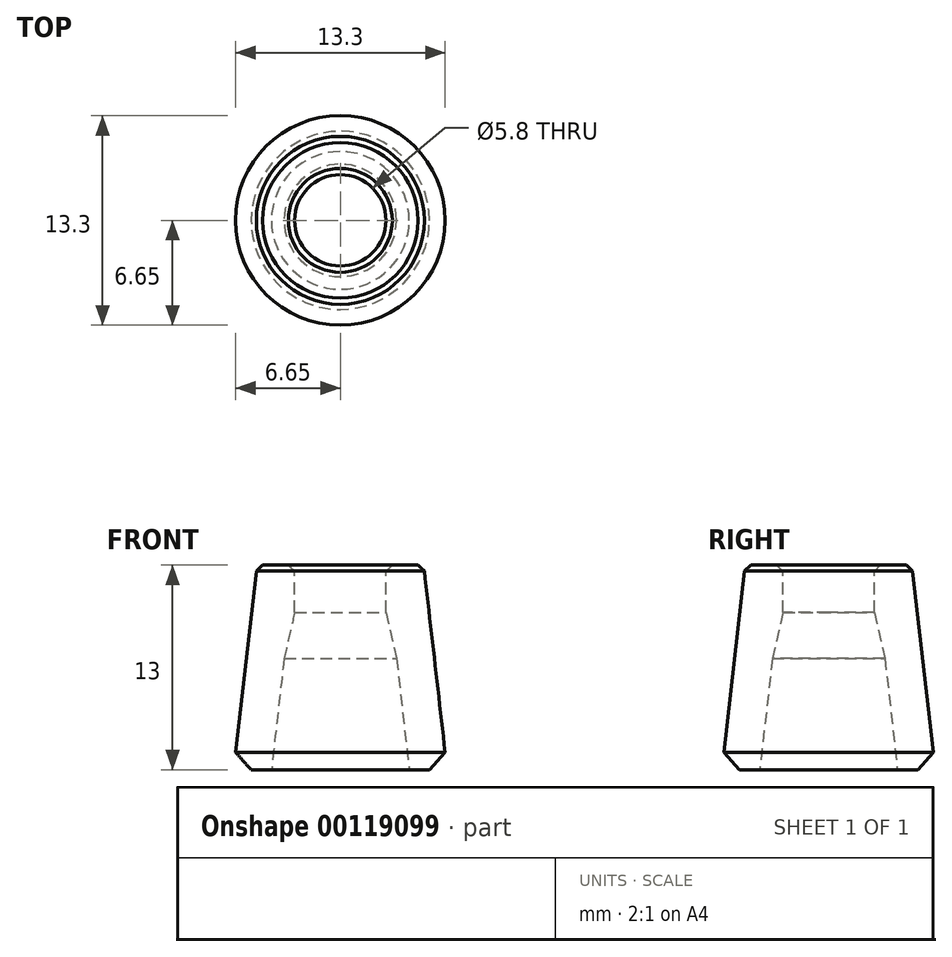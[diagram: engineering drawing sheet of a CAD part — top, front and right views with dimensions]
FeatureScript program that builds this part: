
annotation { "Feature Type Name" : "Feature", "Feature Type Description" : "" }
export const myFeature = defineFeature(function(context is Context, id is Id, definition is map)
    precondition{}
    {
        {
            var Q0;
            Q0=qCreatedBy(makeId("Front.planeOp"),FACE);
            var sketch = newSketch(context, id + "F0", { "sketchPlane" : qUnion([Q0])});
            skLineSegment(sketch, "E0", {"start": v(0, 0) * mm, "end": v(0, 13) * mm, "construction": true});
            skLineSegment(sketch, "E1", {"start": v(2.9, 0) * mm, "end": v(5.3, 0) * mm});
            skLineSegment(sketch, "E2", {"start": v(4.38, 13) * mm, "end": v(3.57, 5.92) * mm});
            skPoint(sketch, "E3.visualSharp", {"position": v(4.37, 13) * mm});
            skLineSegment(sketch, "E4.0", {"start": v(6.78, 13) * mm, "end": v(5.3, 0) * mm});
            skLineSegment(sketch, "E5", {"start": v(2.9, 0) * mm, "end": v(2.9, 3) * mm});
            skLineSegment(sketch, "E6", {"start": v(2.9, 3) * mm, "end": v(3.57, 5.92) * mm});
            skLineSegment(sketch, "E7", {"start": v(4.37, 13) * mm, "end": v(6.78, 13) * mm});
            skPoint(sketch, "E8.orphan", {"position": v(4.24, 11.85) * mm});
            skLineSegment(sketch, "E9", {"start": v(6.78, 13) * mm, "end": v(19.88, 13) * mm, "construction": true});
            skSolve(sketch);
        }
        {
            var Q0;
            Q0=makeQuery(id+"F0.imprint","IMPRINT",FACE,{"disambiguationData":[TD([[makeQuery(id+"F0.imprint","IMPRINT",EDGE,{"derivedFrom":sQuery(id+"F0.wireOp",EDGE,"E1")}),1.0]])]});
            var Q1;
            Q1=sQuery(id+"F0.wireOp",EDGE,"E0");
            revolve(context, id + "F1", {"entities" : qUnion([Q0]), "axis" : qUnion([Q1]), "revolveType" : RevolveType.FULL});
        }
        {
            var Q0;
            Q0=makeQuery(id+"F1.opRevolve","SWEPT_EDGE",EDGE,{"disambiguationData":[OSD([sQuery(id+"F0.wireOp",EDGE,"E4.0"),sQuery(id+"F0.wireOp",EDGE,"E7")])]});
            chamfer(context, id + "F2", {"entities" : qUnion([Q0]), "width" : 1 * mm, "tangentPropagation" : true});
        }
        {
            var Q0;
            Q0=makeQuery(id+"F1.opRevolve","SWEPT_EDGE",EDGE,{"disambiguationData":[OSD([sQuery(id+"F0.wireOp",EDGE,"E1"),sQuery(id+"F0.wireOp",EDGE,"E5")])]});
            var Q1;
            Q1=makeQuery(id+"F1.opRevolve","SWEPT_EDGE",EDGE,{"disambiguationData":[OSD([sQuery(id+"F0.wireOp",EDGE,"E1"),sQuery(id+"F0.wireOp",EDGE,"E4.0")])]});
            chamfer(context, id + "F3", {"entities" : qUnion([Q0, Q1]), "width" : .4 * mm, "tangentPropagation" : true});
        }
        {
            var Q0;
            Q0=makeQuery(id+"F1.opRevolve","SWEPT_BODY",BODY,{"disambiguationData":[OSD([sQuery(id+"F0.wireOp",EDGE,"E1"),sQuery(id+"F0.wireOp",EDGE,"E2"),sQuery(id+"F0.wireOp",EDGE,"E4.0"),sQuery(id+"F0.wireOp",EDGE,"E5"),sQuery(id+"F0.wireOp",EDGE,"E6"),sQuery(id+"F0.wireOp",EDGE,"E7")])]});
            var Q1;
            Q1=sQuery(id+"F0.wireOp",EDGE,"E9");
            transform(context, id + "F4", {"entities" : qUnion([Q0]), "transformType" : TransformType.ROTATION, "transformAxis" : qUnion([Q1]), "angle" : 180 * degree, "makeCopy" : false});
        }
        {
            var Q0;
            Q0=makeQuery(id+"F1.opRevolve","SWEPT_BODY",BODY,{"disambiguationData":[OSD([sQuery(id+"F0.wireOp",EDGE,"E1"),sQuery(id+"F0.wireOp",EDGE,"E2"),sQuery(id+"F0.wireOp",EDGE,"E4.0"),sQuery(id+"F0.wireOp",EDGE,"E5"),sQuery(id+"F0.wireOp",EDGE,"E6"),sQuery(id+"F0.wireOp",EDGE,"E7")])]});
            var Q1;
            Q1=sQuery(id+"F0.wireOp",EDGE,"E0");
            transform(context, id + "F5", {"entities" : qUnion([Q0]), "transformType" : TransformType.TRANSLATION_ENTITY, "oppositeDirectionEntity" : true, "transformLine" : qUnion([Q1]), "makeCopy" : false});
        }
    });
